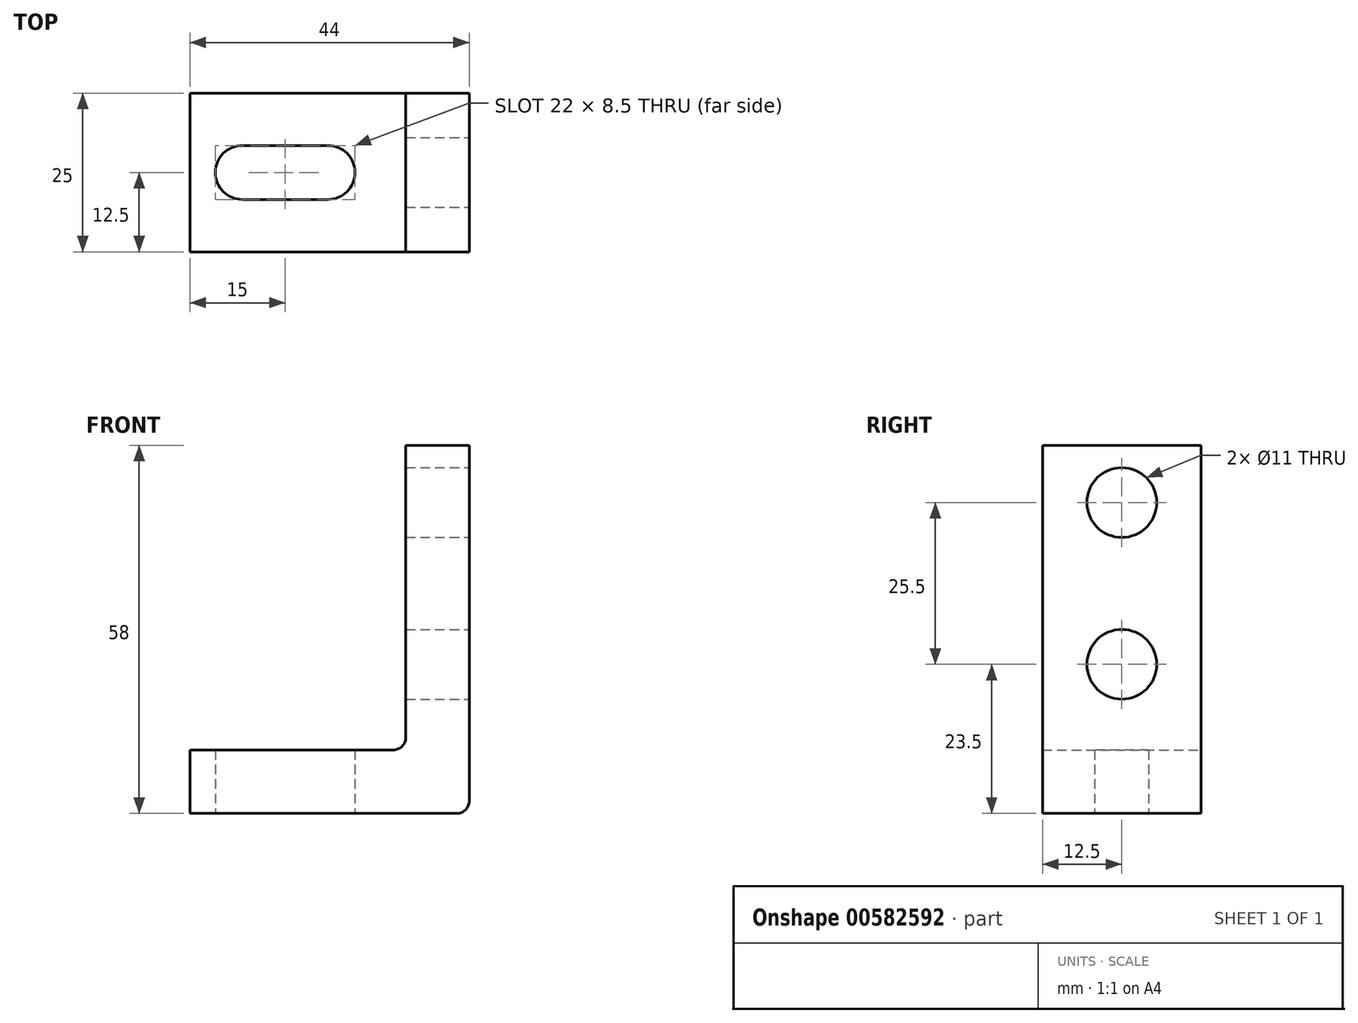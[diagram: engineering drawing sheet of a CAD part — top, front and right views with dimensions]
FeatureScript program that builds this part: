
annotation { "Feature Type Name" : "Feature", "Feature Type Description" : "" }
export const myFeature = defineFeature(function(context is Context, id is Id, definition is map)
    precondition{}
    {
        {
            var Q0;
            Q0=qCreatedBy(makeId("Front.planeOp"),FACE);
            var sketch = newSketch(context, id + "F0", { "sketchPlane" : qUnion([Q0])});
            skLineSegment(sketch, "E0", {"start": v(0, 48) * mm, "end": v(10, 48) * mm});
            skLineSegment(sketch, "E1", {"start": v(10, 48) * mm, "end": v(10, -10) * mm});
            skLineSegment(sketch, "E2", {"start": v(10, -10) * mm, "end": v(-34, -10) * mm});
            skLineSegment(sketch, "E3", {"start": v(-34, -10) * mm, "end": v(-34, 0) * mm});
            skLineSegment(sketch, "E4", {"start": v(-34, 0) * mm, "end": v(0, 0) * mm});
            skLineSegment(sketch, "E5", {"start": v(0, 0) * mm, "end": v(0, 48) * mm});
            skSolve(sketch);
        }
        {
            var Q0;
            Q0 = qSketchRegion(id + "F0", true);
            extrude(context, id + "F1", {"entities" : qUnion([Q0]), "depth" : 25 * mm, "offsetDistance" : 25 * mm});
        }
        {
            var Q0;
            Q0=makeQuery(id+"F1.opExtrude","SWEPT_FACE",FACE,{"disambiguationData":[OSD([sQuery(id+"F0.wireOp",EDGE,"E2")])]});
            var sketch = newSketch(context, id + "F2", { "sketchPlane" : qUnion([Q0])});
            skArc(sketch, "E6", {"start": v(-25.75, 16.75) * mm, "mid": v(-30, 12.5) * mm, "end": v(-25.75, 8.25) * mm});
            skArc(sketch, "E7", {"start": v(-12.25, 8.25) * mm, "mid": v(-8, 12.5) * mm, "end": v(-12.25, 16.75) * mm});
            skLineSegment(sketch, "E8", {"start": v(-25.75, 16.75) * mm, "end": v(-12.25, 16.75) * mm});
            skLineSegment(sketch, "E9", {"start": v(-25.75, 8.25) * mm, "end": v(-12.25, 8.25) * mm});
            skPoint(sketch, "E10.trimOffspring.end.orphan", {"position": v(10, 12.5) * mm});
            skPoint(sketch, "E11.start.orphan", {"position": v(-34, 12.5) * mm});
            skSolve(sketch);
        }
        {
            var Q0;
            Q0=makeQuery(id+"F2.imprint","IMPRINT",FACE,{"disambiguationData":[TD([[makeQuery(id+"F2.imprint","IMPRINT",EDGE,{"derivedFrom":sQuery(id+"F2.wireOp",EDGE,"E6")}),1.0]])]});
            extrude(context, id + "F3", {"entities" : qUnion([Q0]), "operationType" : NewBodyOperationType.REMOVE, "oppositeDirection" : true, "depth" : 10 * mm, "offsetDistance" : 25 * mm});
        }
        {
            var Q0;
            Q0=makeQuery(id+"F1.opExtrude","SWEPT_FACE",FACE,{"disambiguationData":[OSD([sQuery(id+"F0.wireOp",EDGE,"E1")])]});
            var sketch = newSketch(context, id + "F4", { "sketchPlane" : qUnion([Q0])});
            skCircle(sketch, "E12", {"center": v(-12.5, 13.5) * mm, "radius": 5.5 * mm});
            skCircle(sketch, "E13", {"center": v(-12.5, 39) * mm, "radius": 5.5 * mm});
            skSolve(sketch);
        }
        {
            var Q0;
            Q0 = qSketchRegion(id + "F4", true);
            extrude(context, id + "F5", {"entities" : qUnion([Q0]), "operationType" : NewBodyOperationType.REMOVE, "oppositeDirection" : true, "depth" : 10 * mm, "offsetDistance" : 25 * mm});
        }
        {
            var Q0;
            Q0=makeQuery(id+"F1.opExtrude","SWEPT_EDGE",EDGE,{"disambiguationData":[OSD([sQuery(id+"F0.wireOp",EDGE,"E4"),sQuery(id+"F0.wireOp",EDGE,"E5")])]});
            fillet(context, id + "F6", {"entities" : qUnion([Q0]), "radius" : 2 * mm, "tangentPropagation" : true, "allowEdgeOverflow" : false});
        }
        {
            var Q0;
            Q0=makeQuery(id+"F1.opExtrude","SWEPT_EDGE",EDGE,{"disambiguationData":[OSD([sQuery(id+"F0.wireOp",EDGE,"E1"),sQuery(id+"F0.wireOp",EDGE,"E2")])]});
            fillet(context, id + "F7", {"entities" : qUnion([Q0]), "radius" : 2 * mm, "tangentPropagation" : true, "allowEdgeOverflow" : false});
        }
    });
